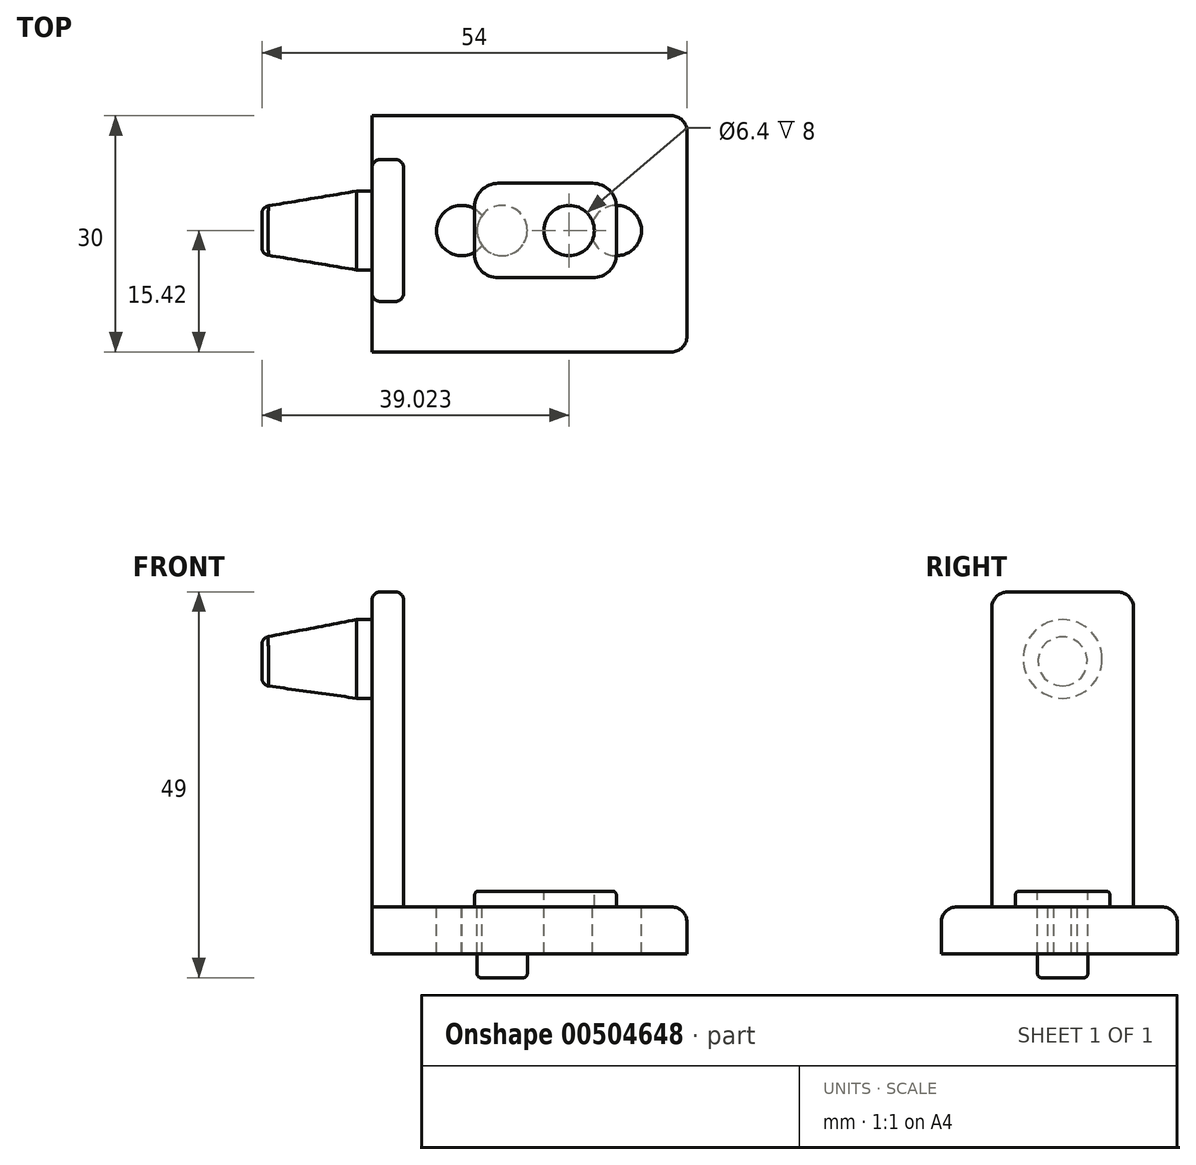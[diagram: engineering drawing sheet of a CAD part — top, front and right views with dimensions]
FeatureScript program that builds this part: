
annotation { "Feature Type Name" : "Feature", "Feature Type Description" : "" }
export const myFeature = defineFeature(function(context is Context, id is Id, definition is map)
    precondition{}
    {
        {
            var Q0;
            Q0=qCreatedBy(makeId("Top.planeOp"),FACE);
            var sketch = newSketch(context, id + "F0", { "sketchPlane" : qUnion([Q0])});
            skLineSegment(sketch, "E0.bottom", {"start": v(0, 14.58) * mm, "end": v(40, 14.58) * mm});
            skLineSegment(sketch, "E0.top", {"start": v(0, -15.42) * mm, "end": v(40, -15.42) * mm});
            skLineSegment(sketch, "E0.left", {"start": v(0, 14.58) * mm, "end": v(0, -15.42) * mm});
            skLineSegment(sketch, "E0.right", {"start": v(40, 14.58) * mm, "end": v(40, -15.42) * mm});
            skSolve(sketch);
        }
        {
            var Q0;
            Q0=qSketchRegion(id+"F0",true);
            extrude(context, id + "F1", {"entities" : qUnion([Q0]), "depth" : 6 * mm});
        }
        {
            var Q0;
            Q0=makeQuery(id+"F1.opExtrude","CAP_FACE",FACE,{"disambiguationData":[OSD([sQuery(id+"F0.wireOp",EDGE,"E0.bottom"),sQuery(id+"F0.wireOp",EDGE,"E0.top"),sQuery(id+"F0.wireOp",EDGE,"E0.left"),sQuery(id+"F0.wireOp",EDGE,"E0.right")])],"isStart":false});
            var sketch = newSketch(context, id + "F2", { "sketchPlane" : qUnion([Q0])});
            skLineSegment(sketch, "E1.bottom", {"start": v(0, 9) * mm, "end": v(4, 9) * mm});
            skLineSegment(sketch, "E1.top", {"start": v(0, -9) * mm, "end": v(4, -9) * mm});
            skLineSegment(sketch, "E1.left", {"start": v(0, 9) * mm, "end": v(0, -9) * mm});
            skLineSegment(sketch, "E1.right", {"start": v(4, 9) * mm, "end": v(4, -9) * mm});
            skSolve(sketch);
        }
        {
            var Q0;
            Q0=makeQuery(id+"F2.imprint","IMPRINT",FACE,{"disambiguationData":[TD([[makeQuery(id+"F2.imprint","IMPRINT",EDGE,{"derivedFrom":sQuery(id+"F2.wireOp",EDGE,"E1.bottom")}),-1.0]])]});
            extrude(context, id + "F3", {"entities" : qUnion([Q0]), "operationType" : NewBodyOperationType.ADD, "depth" : 40 * mm});
        }
        {
            var Q0;
            Q0=makeQuery(id+"F3.opExtrude","SWEPT_FACE",FACE,{"disambiguationData":[OSD([sQuery(id+"F2.wireOp",EDGE,"E1.right")])]});
            var sketch = newSketch(context, id + "F4", { "sketchPlane" : qUnion([Q0])});
            skLineSegment(sketch, "E2", {"start": v(0, 46) * mm, "end": v(0, 6) * mm, "construction": true});
            skLineSegment(sketch, "E3", {"start": v(-9, 37.5) * mm, "end": v(9, 37.5) * mm});
            skCircle(sketch, "E4", {"center": v(0, 37.5) * mm, "radius": 5 * mm});
            skSolve(sketch);
        }
        {
            var Q0;
            Q0=qSketchRegion(id+"F4",true);
            extrude(context, id + "F5", {"entities" : qUnion([Q0]), "operationType" : NewBodyOperationType.ADD, "oppositeDirection" : true, "depth" : 6 * mm});
        }
        {
            var Q0;
            Q0=makeQuery(id+"F5.opExtrude","CAP_FACE",FACE,{"disambiguationData":[OSD([sQuery(id+"F4.wireOp",EDGE,"E4")])],"isStart":false});
            cPlane(context, id + "F6", {"entities" : qUnion([Q0]), "cplaneType" : CPlaneType.OFFSET, "offset" : 12 * mm, "width" : 150 * mm, "height" : 150 * mm});
        }
        {
            var Q0;
            Q0=qCreatedBy(id+"F6.planeOp",FACE);
            var sketch = newSketch(context, id + "F7", { "sketchPlane" : qUnion([Q0])});
            skLineSegment(sketch, "E5", {"start": v(0, 37.17) * mm, "end": v(0, 37.17) * mm});
            skLineSegment(sketch, "E6", {"start": v(0, 37.17) * mm, "end": v(-8.55, 37.17) * mm, "construction": true});
            skCircle(sketch, "E7", {"center": v(0, 37.17) * mm, "radius": 3 * mm});
            skSolve(sketch);
        }
        {
            var Q0;
            Q0=makeQuery(id+"F5.opExtrude","CAP_FACE",FACE,{"disambiguationData":[OSD([sQuery(id+"F4.wireOp",EDGE,"E4")])],"isStart":false});
            var Q1;
            Q1=makeQuery(id+"F7.imprint","IMPRINT",FACE,{"disambiguationData":[TD([[makeQuery(id+"F7.imprint","IMPRINT",EDGE,{"derivedFrom":sQuery(id+"F7.wireOp",EDGE,"E7")}),1.0]])]});
            loft(context, id + "F8", {"sheetProfilesArray" : [{ "sheetProfileEntities" : qUnion([Q0]) }, { "sheetProfileEntities" : qUnion([Q1]) }]});
        }
        {
            var Q0;
            Q0=makeQuery(id+"F1.opExtrude","CAP_FACE",FACE,{"disambiguationData":[OSD([sQuery(id+"F0.wireOp",EDGE,"E0.bottom"),sQuery(id+"F0.wireOp",EDGE,"E0.top"),sQuery(id+"F0.wireOp",EDGE,"E0.left"),sQuery(id+"F0.wireOp",EDGE,"E0.right")])],"isStart":false});
            var sketch = newSketch(context, id + "F9", { "sketchPlane" : qUnion([Q0])});
            skCircle(sketch, "E8", {"center": v(11.38, 0) * mm, "radius": 3.2 * mm});
            skCircle(sketch, "E9", {"center": v(31.02, 0) * mm, "radius": 3.2 * mm});
            skLineSegment(sketch, "E10", {"start": v(11.34, 3.2) * mm, "end": v(31.02, 3.2) * mm});
            skLineSegment(sketch, "E11", {"start": v(11.67, -3.19) * mm, "end": v(31.02, -3.2) * mm});
            skSolve(sketch);
        }
        {
            var Q0;
            {var subQ0=sQuery(id+"F9.wireOp",EDGE,"E9");var subQ1=makeQuery(id+"F9.imprint","INTERSECT",VERTEX,{"derivedFrom":[subQ0,sQuery(id+"F9.wireOp",EDGE,"E10")]});Q0=makeQuery(id+"F9.imprint","IMPRINT",FACE,{"disambiguationData":[TD([[makeQuery(id+"F9.imprint","IMPRINT",EDGE,{"disambiguationData":[TD([[subQ1,-1.0]])],"derivedFrom":subQ0}),1.0]])]});}
            var Q1;
            {var subQ0=sQuery(id+"F9.wireOp",EDGE,"E10");Q1=makeQuery(id+"F9.imprint","IMPRINT",FACE,{"disambiguationData":[TD([[makeQuery(id+"F9.imprint","IMPRINT",EDGE,{"derivedFrom":subQ0}),-1.0]])]});}
            var Q2;
            {var subQ0=sQuery(id+"F9.wireOp",EDGE,"E8");var subQ2=makeQuery(id+"F9.imprint","IMPRINT",VERTEX,{"derivedFrom":subQ0});Q2=makeQuery(id+"F9.imprint","IMPRINT",FACE,{"disambiguationData":[TD([[makeQuery(id+"F9.imprint","IMPRINT",EDGE,{"disambiguationData":[TD([[subQ2,1.0]])],"derivedFrom":subQ0}),1.0]])]});}
            extrude(context, id + "F10", {"entities" : qUnion([Q0, Q1, Q2]), "operationType" : NewBodyOperationType.REMOVE, "endBound" : BoundingType.THROUGH_ALL, "oppositeDirection" : true, "depth" : 25 * mm});
        }
        {
            var Q0;
            Q0=makeQuery(id+"F3.opExtrude","CAP_EDGE",EDGE,{"disambiguationData":[OSD([sQuery(id+"F2.wireOp",EDGE,"E1.right")])],"isStart":false});
            var Q1;
            Q1=makeQuery(id+"F3.opExtrude","SWEPT_EDGE",EDGE,{"disambiguationData":[OSD([sQuery(id+"F2.wireOp",EDGE,"E1.top"),sQuery(id+"F2.wireOp",EDGE,"E1.right")])]});
            var Q2;
            Q2=makeQuery(id+"F3.opExtrude","SWEPT_EDGE",EDGE,{"disambiguationData":[OSD([sQuery(id+"F2.wireOp",EDGE,"E1.bottom"),sQuery(id+"F2.wireOp",EDGE,"E1.right")])]});
            var Q3;
            Q3=makeQuery(id+"F3.opExtrude","CAP_EDGE",EDGE,{"disambiguationData":[OSD([sQuery(id+"F2.wireOp",EDGE,"E1.right")])],"isStart":true});
            var Q4;
            {var subQ0=sQuery(id+"F2.wireOp",EDGE,"E1.top");var subQ1=sQuery(id+"F0.wireOp",EDGE,"E0.left");var subQ2=sQuery(id+"F2.wireOp",EDGE,"E1.left");Q4=makeQuery(id+"F5.boolean.opBoolean","SPLIT",EDGE,{"disambiguationData":[TD([makeQuery(id+"F1.opExtrude","CAP_FACE",FACE,{"disambiguationData":[OSD([sQuery(id+"F0.wireOp",EDGE,"E0.bottom"),sQuery(id+"F0.wireOp",EDGE,"E0.top"),subQ1,sQuery(id+"F0.wireOp",EDGE,"E0.right")])],"isStart":false})])],"derivedFrom":makeQuery(id+"F3.opExtrude","SWEPT_EDGE",EDGE,{"disambiguationData":[OSD([subQ1,subQ0,subQ2])]})});}
            var Q5;
            {var subQ0=sQuery(id+"F2.wireOp",EDGE,"E1.bottom");var subQ1=sQuery(id+"F0.wireOp",EDGE,"E0.left");var subQ2=sQuery(id+"F2.wireOp",EDGE,"E1.left");Q5=makeQuery(id+"F5.boolean.opBoolean","SPLIT",EDGE,{"disambiguationData":[TD([makeQuery(id+"F1.opExtrude","CAP_FACE",FACE,{"disambiguationData":[OSD([sQuery(id+"F0.wireOp",EDGE,"E0.bottom"),sQuery(id+"F0.wireOp",EDGE,"E0.top"),subQ1,sQuery(id+"F0.wireOp",EDGE,"E0.right")])],"isStart":false})])],"derivedFrom":makeQuery(id+"F3.opExtrude","SWEPT_EDGE",EDGE,{"disambiguationData":[OSD([subQ1,subQ0,subQ2])]})});}
            var Q6;
            Q6=makeQuery(id+"F3.opExtrude","CAP_EDGE",EDGE,{"disambiguationData":[OSD([sQuery(id+"F2.wireOp",EDGE,"E1.left")])],"isStart":false});
            var Q7;
            Q7=makeQuery(id+"F8.opLoft","MID_CAP_EDGE",EDGE,{"disambiguationData":[OSD([sQuery(id+"F4.wireOp",EDGE,"E4"),sQuery(id+"F7.wireOp",EDGE,"E7")])],"capPos":1.0});
            fillet(context, id + "F11", {"entities" : qUnion([Q0, Q1, Q2, Q3, Q4, Q5, Q6, Q7]), "radius" : 1 * mm, "tangentPropagation" : true, "allowEdgeOverflow" : false});
        }
        {
            var Q0;
            Q0=makeQuery(id+"F3.opExtrude","CAP_EDGE",EDGE,{"disambiguationData":[OSD([sQuery(id+"F2.wireOp",EDGE,"E1.bottom")])],"isStart":false});
            var Q1;
            Q1=makeQuery(id+"F3.opExtrude","CAP_EDGE",EDGE,{"disambiguationData":[OSD([sQuery(id+"F2.wireOp",EDGE,"E1.top")])],"isStart":false});
            var Q2;
            Q2=makeQuery(id+"F1.opExtrude","CAP_EDGE",EDGE,{"disambiguationData":[OSD([sQuery(id+"F0.wireOp",EDGE,"E0.top")])],"isStart":false});
            var Q3;
            Q3=makeQuery(id+"F1.opExtrude","CAP_EDGE",EDGE,{"disambiguationData":[OSD([sQuery(id+"F0.wireOp",EDGE,"E0.right")])],"isStart":false});
            var Q4;
            Q4=makeQuery(id+"F1.opExtrude","CAP_EDGE",EDGE,{"disambiguationData":[OSD([sQuery(id+"F0.wireOp",EDGE,"E0.bottom")])],"isStart":false});
            var Q5;
            Q5=makeQuery(id+"F1.opExtrude","SWEPT_EDGE",EDGE,{"disambiguationData":[OSD([sQuery(id+"F0.wireOp",EDGE,"E0.top"),sQuery(id+"F0.wireOp",EDGE,"E0.right")])]});
            var Q6;
            Q6=makeQuery(id+"F1.opExtrude","SWEPT_EDGE",EDGE,{"disambiguationData":[OSD([sQuery(id+"F0.wireOp",EDGE,"E0.bottom"),sQuery(id+"F0.wireOp",EDGE,"E0.right")])]});
            fillet(context, id + "F12", {"entities" : qUnion([Q0, Q1, Q2, Q3, Q4, Q5, Q6]), "radius" : 2 * mm, "tangentPropagation" : true, "allowEdgeOverflow" : false});
        }
        {
            var Q0;
            Q0=makeQuery(id+"F1.opExtrude","CAP_FACE",FACE,{"disambiguationData":[OSD([sQuery(id+"F0.wireOp",EDGE,"E0.bottom"),sQuery(id+"F0.wireOp",EDGE,"E0.top"),sQuery(id+"F0.wireOp",EDGE,"E0.left"),sQuery(id+"F0.wireOp",EDGE,"E0.right")])],"isStart":false});
            var sketch = newSketch(context, id + "F13", { "sketchPlane" : qUnion([Q0])});
            skLineSegment(sketch, "E12.bottom", {"start": v(13.02, 6) * mm, "end": v(31.02, 6) * mm});
            skLineSegment(sketch, "E12.top", {"start": v(13.02, -6) * mm, "end": v(31.02, -6) * mm});
            skLineSegment(sketch, "E12.left", {"start": v(13.02, 6) * mm, "end": v(13.02, -6) * mm});
            skLineSegment(sketch, "E12.right", {"start": v(31.02, 6) * mm, "end": v(31.02, -6) * mm});
            skLineSegment(sketch, "E13", {"start": v(13.02, 0) * mm, "end": v(15.02, 0) * mm, "construction": true});
            skLineSegment(sketch, "E14", {"start": v(28.02, 0) * mm, "end": v(31.02, 0) * mm, "construction": true});
            skSolve(sketch);
        }
        {
            var Q0;
            Q0 = qSketchRegion(id + "F13", true);
            extrude(context, id + "F14", {"entities" : qUnion([Q0]), "depth" : 2 * mm});
        }
        {
            var Q0;
            Q0=makeQuery(id+"F14.opExtrude","CAP_FACE",FACE,{"disambiguationData":[OSD([sQuery(id+"F13.wireOp",EDGE,"E12.bottom"),sQuery(id+"F13.wireOp",EDGE,"E12.top"),sQuery(id+"F13.wireOp",EDGE,"E12.left"),sQuery(id+"F13.wireOp",EDGE,"E12.right")])],"isStart":false});
            var sketch = newSketch(context, id + "F15", { "sketchPlane" : qUnion([Q0])});
            skCircle(sketch, "E15", {"center": v(16.52, 0) * mm, "radius": 3.19 * mm});
            skSolve(sketch);
        }
        {
            var Q0;
            Q0 = qSketchRegion(id + "F15", true);
            extrude(context, id + "F16", {"entities" : qUnion([Q0]), "operationType" : NewBodyOperationType.ADD, "oppositeDirection" : true, "depth" : 11 * mm});
        }
        {
            var Q0;
            Q0=makeQuery(id+"F16.boolean.opBoolean","MERGE",FACE,{"derivedFrom":[makeQuery(id+"F14.opExtrude","CAP_FACE",FACE,{"disambiguationData":[OSD([sQuery(id+"F13.wireOp",EDGE,"E12.bottom"),sQuery(id+"F13.wireOp",EDGE,"E12.top"),sQuery(id+"F13.wireOp",EDGE,"E12.left"),sQuery(id+"F13.wireOp",EDGE,"E12.right")])],"isStart":false}),makeQuery(id+"F16.opExtrude","CAP_FACE",FACE,{"disambiguationData":[OSD([sQuery(id+"F15.wireOp",EDGE,"E15")])],"isStart":true})]});
            var sketch = newSketch(context, id + "F17", { "sketchPlane" : qUnion([Q0])});
            skCircle(sketch, "E16", {"center": v(25.02, 0) * mm, "radius": 3.2 * mm});
            skPoint(sketch, "E16.centerSnap0", {"position": v(31.02, 0) * mm});
            skSolve(sketch);
        }
        {
            var Q0;
            Q0 = qSketchRegion(id + "F17", true);
            extrude(context, id + "F18", {"entities" : qUnion([Q0]), "operationType" : NewBodyOperationType.REMOVE, "endBound" : BoundingType.THROUGH_ALL, "oppositeDirection" : true, "depth" : 25 * mm});
        }
        {
            var Q0;
            Q0=makeQuery(id+"F14.opExtrude","SWEPT_EDGE",EDGE,{"disambiguationData":[OSD([sQuery(id+"F13.wireOp",EDGE,"E12.top"),sQuery(id+"F13.wireOp",EDGE,"E12.left")])]});
            var Q1;
            Q1=makeQuery(id+"F14.opExtrude","SWEPT_EDGE",EDGE,{"disambiguationData":[OSD([sQuery(id+"F13.wireOp",EDGE,"E12.top"),sQuery(id+"F13.wireOp",EDGE,"E12.right")])]});
            var Q2;
            Q2=makeQuery(id+"F14.opExtrude","SWEPT_EDGE",EDGE,{"disambiguationData":[OSD([sQuery(id+"F13.wireOp",EDGE,"E12.bottom"),sQuery(id+"F13.wireOp",EDGE,"E12.right")])]});
            var Q3;
            Q3=makeQuery(id+"F14.opExtrude","SWEPT_EDGE",EDGE,{"disambiguationData":[OSD([sQuery(id+"F13.wireOp",EDGE,"E12.bottom"),sQuery(id+"F13.wireOp",EDGE,"E12.left")])]});
            fillet(context, id + "F19", {"entities" : qUnion([Q0, Q1, Q2, Q3]), "radius" : 3 * mm, "tangentPropagation" : true, "allowEdgeOverflow" : false});
        }
        {
            var Q0;
            Q0=makeQuery(id+"F14.opExtrude","CAP_EDGE",EDGE,{"disambiguationData":[OSD([sQuery(id+"F13.wireOp",EDGE,"E12.left")])],"isStart":false});
            var Q1;
            {var subQ0=sQuery(id+"F13.wireOp",EDGE,"E12.left");var subQ1=sQuery(id+"F13.wireOp",EDGE,"E12.top");Q1=makeQuery(id+"F19.opFillet","BLEND_EDGE",EDGE,{"blendedFrom":[makeQuery(id+"F14.opExtrude","SWEPT_EDGE",EDGE,{"disambiguationData":[OSD([subQ1,subQ0])]}),makeQuery(id+"F14.opExtrude","CAP_FACE",FACE,{"disambiguationData":[OSD([sQuery(id+"F13.wireOp",EDGE,"E12.bottom"),subQ1,subQ0,sQuery(id+"F13.wireOp",EDGE,"E12.right")])],"isStart":false})],"blendedInto":[makeQuery(id+"F14.opExtrude","CAP_FACE",FACE,{"disambiguationData":[OSD([sQuery(id+"F13.wireOp",EDGE,"E12.bottom"),subQ1,subQ0,sQuery(id+"F13.wireOp",EDGE,"E12.right")])],"isStart":false})]});}
            var Q2;
            {var subQ0=sQuery(id+"F13.wireOp",EDGE,"E12.right");var subQ1=sQuery(id+"F13.wireOp",EDGE,"E12.top");Q2=makeQuery(id+"F19.opFillet","BLEND_EDGE",EDGE,{"blendedFrom":[makeQuery(id+"F14.opExtrude","SWEPT_EDGE",EDGE,{"disambiguationData":[OSD([subQ1,subQ0])]}),makeQuery(id+"F14.opExtrude","CAP_FACE",FACE,{"disambiguationData":[OSD([sQuery(id+"F13.wireOp",EDGE,"E12.bottom"),subQ1,sQuery(id+"F13.wireOp",EDGE,"E12.left"),subQ0])],"isStart":false})],"blendedInto":[makeQuery(id+"F14.opExtrude","CAP_FACE",FACE,{"disambiguationData":[OSD([sQuery(id+"F13.wireOp",EDGE,"E12.bottom"),subQ1,sQuery(id+"F13.wireOp",EDGE,"E12.left"),subQ0])],"isStart":false})]});}
            var Q3;
            Q3=makeQuery(id+"F14.opExtrude","CAP_EDGE",EDGE,{"disambiguationData":[OSD([sQuery(id+"F13.wireOp",EDGE,"E12.right")])],"isStart":false});
            var Q4;
            {var subQ0=sQuery(id+"F13.wireOp",EDGE,"E12.right");var subQ1=sQuery(id+"F13.wireOp",EDGE,"E12.bottom");Q4=makeQuery(id+"F19.opFillet","BLEND_EDGE",EDGE,{"blendedFrom":[makeQuery(id+"F14.opExtrude","SWEPT_EDGE",EDGE,{"disambiguationData":[OSD([subQ1,subQ0])]}),makeQuery(id+"F14.opExtrude","CAP_FACE",FACE,{"disambiguationData":[OSD([subQ1,sQuery(id+"F13.wireOp",EDGE,"E12.top"),sQuery(id+"F13.wireOp",EDGE,"E12.left"),subQ0])],"isStart":false})],"blendedInto":[makeQuery(id+"F14.opExtrude","CAP_FACE",FACE,{"disambiguationData":[OSD([subQ1,sQuery(id+"F13.wireOp",EDGE,"E12.top"),sQuery(id+"F13.wireOp",EDGE,"E12.left"),subQ0])],"isStart":false})]});}
            var Q5;
            Q5=makeQuery(id+"F14.opExtrude","CAP_EDGE",EDGE,{"disambiguationData":[OSD([sQuery(id+"F13.wireOp",EDGE,"E12.bottom")])],"isStart":false});
            var Q6;
            {var subQ0=sQuery(id+"F13.wireOp",EDGE,"E12.left");var subQ1=sQuery(id+"F13.wireOp",EDGE,"E12.bottom");Q6=makeQuery(id+"F19.opFillet","BLEND_EDGE",EDGE,{"blendedFrom":[makeQuery(id+"F14.opExtrude","SWEPT_EDGE",EDGE,{"disambiguationData":[OSD([subQ1,subQ0])]}),makeQuery(id+"F14.opExtrude","CAP_FACE",FACE,{"disambiguationData":[OSD([subQ1,sQuery(id+"F13.wireOp",EDGE,"E12.top"),subQ0,sQuery(id+"F13.wireOp",EDGE,"E12.right")])],"isStart":false})],"blendedInto":[makeQuery(id+"F14.opExtrude","CAP_FACE",FACE,{"disambiguationData":[OSD([subQ1,sQuery(id+"F13.wireOp",EDGE,"E12.top"),subQ0,sQuery(id+"F13.wireOp",EDGE,"E12.right")])],"isStart":false})]});}
            var Q7;
            Q7=makeQuery(id+"F16.opExtrude","CAP_EDGE",EDGE,{"disambiguationData":[OSD([sQuery(id+"F15.wireOp",EDGE,"E15")])],"isStart":false});
            fillet(context, id + "F20", {"entities" : qUnion([Q0, Q1, Q2, Q3, Q4, Q5, Q6, Q7]), "radius" : .5 * mm, "tangentPropagation" : true, "allowEdgeOverflow" : false});
        }
    });
